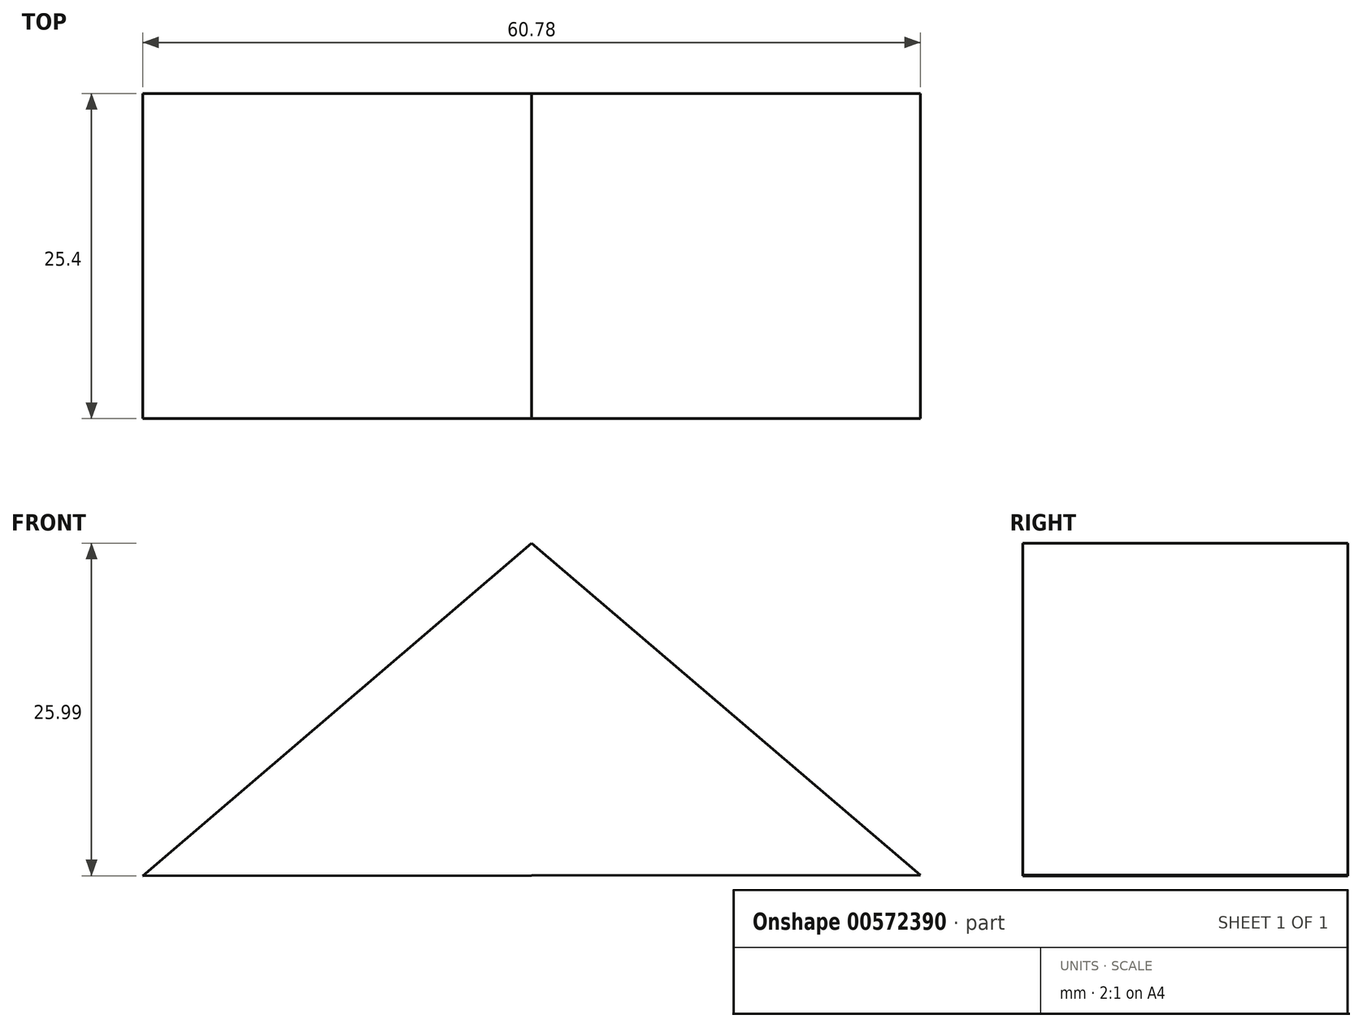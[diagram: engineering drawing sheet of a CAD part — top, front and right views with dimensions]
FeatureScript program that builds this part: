
annotation { "Feature Type Name" : "Feature", "Feature Type Description" : "" }
export const myFeature = defineFeature(function(context is Context, id is Id, definition is map)
    precondition{}
    {
        {
            var Q0;
            Q0=qCreatedBy(makeId("Front.planeOp"),FACE);
            var sketch = newSketch(context, id + "F0", { "sketchPlane" : qUnion([Q0])});
            skLineSegment(sketch, "E0", {"start": v(-61, 25.4) * mm, "end": v(-14.15, 62.64) * mm});
            skLineSegment(sketch, "E1", {"start": v(-14.15, 62.64) * mm, "end": v(32.7, 25.4) * mm});
            skLineSegment(sketch, "E2", {"start": v(32.7, 25.4) * mm, "end": v(32.7, -21.86) * mm});
            skLineSegment(sketch, "E3", {"start": v(32.7, -21.86) * mm, "end": v(-61, -21.86) * mm});
            skLineSegment(sketch, "E4", {"start": v(-61, -21.86) * mm, "end": v(-61, 25.4) * mm});
            skSolve(sketch);
        }
        {
            var Q0;
            Q0=makeQuery(id+"F0.imprint","IMPRINT",FACE,{"disambiguationData":[TD([[makeQuery(id+"F0.imprint","IMPRINT",EDGE,{"derivedFrom":sQuery(id+"F0.wireOp",EDGE,"E0")}),-1.0]])]});
            var sketch = newSketch(context, id + "F1", { "sketchPlane" : qUnion([Q0])});
            skLineSegment(sketch, "E5", {"start": v(-44.1, 26.28) * mm, "end": v(-13.72, 52.27) * mm});
            skLineSegment(sketch, "E6", {"start": v(-13.72, 52.27) * mm, "end": v(16.69, 26.33) * mm});
            skLineSegment(sketch, "E7", {"start": v(16.69, 26.33) * mm, "end": v(-44.1, 26.28) * mm});
            skSolve(sketch);
        }
        {
            var Q0;
            Q0=sQuery(id+"F1.wireOp",EDGE,"E7");
            var Q1;
            Q1=sQuery(id+"F1.wireOp",EDGE,"E5");
            var Q2;
            Q2=sQuery(id+"F1.wireOp",EDGE,"E6");
            extrude(context, id + "F2", {"bodyType" : ToolBodyType.SURFACE, "surfaceEntities" : qUnion([Q0, Q1, Q2]), "depth" : 25.4 * mm, "offsetDistance" : 25.4 * mm});
        }
    });
